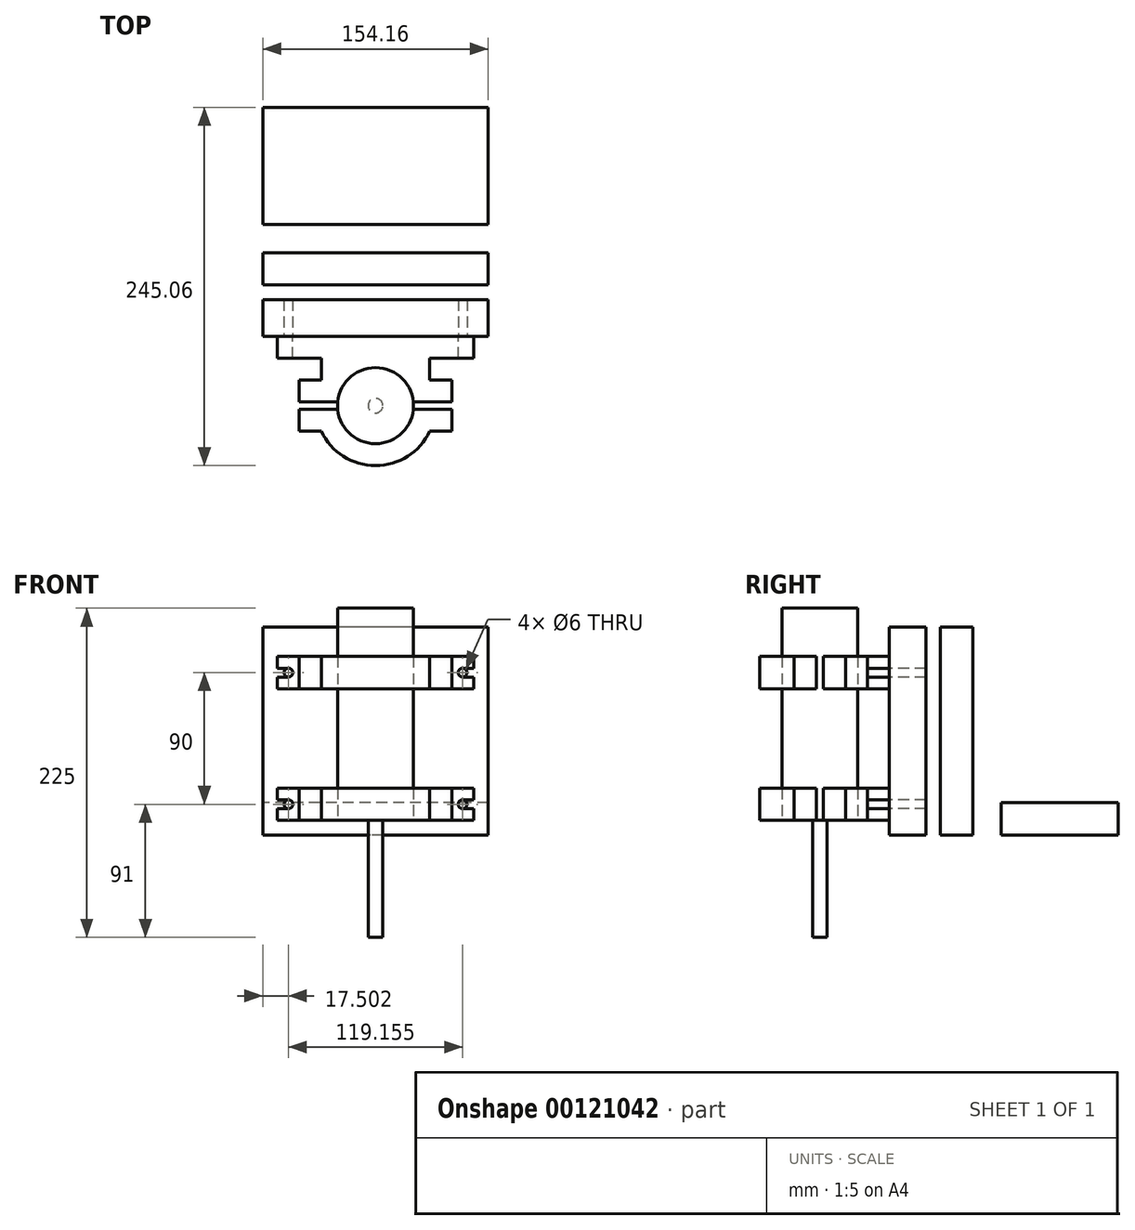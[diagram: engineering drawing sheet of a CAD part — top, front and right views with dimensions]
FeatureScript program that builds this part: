
annotation { "Feature Type Name" : "Feature", "Feature Type Description" : "" }
export const myFeature = defineFeature(function(context is Context, id is Id, definition is map)
    precondition{}
    {
        {
            var Q0;
            Q0=qCreatedBy(makeId("Top.planeOp"),FACE);
            var sketch = newSketch(context, id + "F0", { "sketchPlane" : qUnion([Q0])});
            skCircle(sketch, "E0", {"center": v(0, 0) * mm, "radius": 5 * mm});
            skCircle(sketch, "E1", {"center": v(0, 0) * mm, "radius": 26 * mm});
            skSolve(sketch);
        }
        {
            var Q0;
            Q0=makeQuery(id+"F0.imprint","IMPRINT",FACE,{"disambiguationData":[TD([[makeQuery(id+"F0.imprint","IMPRINT",EDGE,{"derivedFrom":sQuery(id+"F0.wireOp",EDGE,"E0")}),-1.0]])]});
            var Q1;
            Q1=makeQuery(id+"F0.imprint","IMPRINT",FACE,{"disambiguationData":[TD([[makeQuery(id+"F0.imprint","IMPRINT",EDGE,{"derivedFrom":sQuery(id+"F0.wireOp",EDGE,"E0")}),1.0]])]});
            extrude(context, id + "F1", {"entities" : qUnion([Q0, Q1]), "depth" : 145 * mm});
        }
        {
            var Q0;
            Q0=makeQuery(id+"F0.imprint","IMPRINT",FACE,{"disambiguationData":[TD([[makeQuery(id+"F0.imprint","IMPRINT",EDGE,{"derivedFrom":sQuery(id+"F0.wireOp",EDGE,"E0")}),1.0]])]});
            extrude(context, id + "F2", {"entities" : qUnion([Q0]), "operationType" : NewBodyOperationType.ADD, "oppositeDirection" : true, "depth" : 80 * mm});
        }
        {
            var Q0;
            Q0=qCreatedBy(makeId("Top.planeOp"),FACE);
            var sketch = newSketch(context, id + "F3", { "sketchPlane" : qUnion([Q0])});
            skArc(sketch, "E2.0", {"start": v(-25.88, -2.5) * mm, "mid": v(0, -26) * mm, "end": v(25.88, -2.5) * mm});
            skLineSegment(sketch, "E3", {"start": v(-25.88, -2.5) * mm, "end": v(-52.08, -2.5) * mm});
            skLineSegment(sketch, "E4", {"start": v(-52.08, -2.5) * mm, "end": v(-52.08, -17.5) * mm});
            skLineSegment(sketch, "E5", {"start": v(-52.08, -17.5) * mm, "end": v(-37.08, -17.5) * mm});
            skArc(sketch, "E6", {"start": v(-37.08, -17.5) * mm, "mid": v(-21.95, -34.63) * mm, "end": v(0, -41) * mm});
            skLineSegment(sketch, "E7", {"start": v(-25.88, 2.5) * mm, "end": v(-52.08, 2.5) * mm});
            skLineSegment(sketch, "E8", {"start": v(-52.08, 2.5) * mm, "end": v(-52.08, 17.5) * mm});
            skLineSegment(sketch, "E9", {"start": v(-52.08, 17.5) * mm, "end": v(-37.08, 17.5) * mm});
            skLineSegment(sketch, "E10", {"start": v(-37.08, 17.5) * mm, "end": v(-37.08, 32.5) * mm});
            skLineSegment(sketch, "E11", {"start": v(-37.08, 32.5) * mm, "end": v(-67.08, 32.5) * mm});
            skLineSegment(sketch, "E12", {"start": v(-67.08, 32.5) * mm, "end": v(-67.08, 47.5) * mm});
            skLineSegment(sketch, "E13", {"start": v(-67.08, 47.5) * mm, "end": v(0, 47.5) * mm});
            skLineSegment(sketch, "E14.MirrorCS", {"start": v(52.08, 17.5) * mm, "end": v(37.08, 17.5) * mm});
            skLineSegment(sketch, "E15.MirrorCS", {"start": v(37.08, 17.5) * mm, "end": v(37.08, 32.5) * mm});
            skLineSegment(sketch, "E16.MirrorCS", {"start": v(52.08, 2.5) * mm, "end": v(52.08, 17.5) * mm});
            skLineSegment(sketch, "E17.MirrorCS", {"start": v(37.08, 32.5) * mm, "end": v(67.08, 32.5) * mm});
            skLineSegment(sketch, "E18.MirrorCS", {"start": v(25.88, 2.5) * mm, "end": v(52.08, 2.5) * mm});
            skLineSegment(sketch, "E19.MirrorCS", {"start": v(67.08, 32.5) * mm, "end": v(67.08, 47.5) * mm});
            skLineSegment(sketch, "E20.MirrorCS", {"start": v(52.08, -17.5) * mm, "end": v(37.08, -17.5) * mm});
            skLineSegment(sketch, "E21.MirrorCS", {"start": v(52.08, -2.5) * mm, "end": v(52.08, -17.5) * mm});
            skLineSegment(sketch, "E22.MirrorCS", {"start": v(25.88, -2.5) * mm, "end": v(52.08, -2.5) * mm});
            skLineSegment(sketch, "E23.MirrorCS", {"start": v(67.08, 47.5) * mm, "end": v(0, 47.5) * mm});
            skArc(sketch, "E24.MirrorCS", {"start": v(37.08, -17.5) * mm, "mid": v(21.95, -34.63) * mm, "end": v(0, -41) * mm});
            skArc(sketch, "E25.trimOffspring", {"start": v(25.88, 2.5) * mm, "mid": v(0, 26) * mm, "end": v(-25.88, 2.5) * mm});
            skSolve(sketch);
        }
        {
            var Q0;
            Q0 = qSketchRegion(id + "F3", true);
            extrude(context, id + "F4", {"entities" : qUnion([Q0]), "depth" : 22 * mm});
        }
        {
            var Q0;
            Q0=makeQuery(id+"F4.opExtrude","SWEPT_FACE",FACE,{"disambiguationData":[OSD([sQuery(id+"F3.wireOp",EDGE,"E13"),sQuery(id+"F3.wireOp",EDGE,"E23.MirrorCS")])]});
            var sketch = newSketch(context, id + "F5", { "sketchPlane" : qUnion([Q0])});
            skLineSegment(sketch, "E26.0", {"start": v(-52.08, 22) * mm, "end": v(-52.08, 0) * mm, "construction": true});
            skLineSegment(sketch, "E27.0.0", {"start": v(-67.08, 0) * mm, "end": v(-62.58, 0) * mm, "construction": true});
            skLineSegment(sketch, "E27.0.1", {"start": v(67.08, 0) * mm, "end": v(67.08, 22) * mm, "construction": true});
            skLineSegment(sketch, "E27.0.2", {"start": v(67.08, 22) * mm, "end": v(-67.08, 22) * mm, "construction": true});
            skLineSegment(sketch, "E27.0.3", {"start": v(-67.08, 22) * mm, "end": v(-67.08, 0) * mm, "construction": true});
            skLineSegment(sketch, "E28", {"start": v(-67.08, 11) * mm, "end": v(-52.08, 11) * mm, "construction": true});
            skArc(sketch, "E29", {"start": v(-56.58, 11) * mm, "mid": v(-59.58, 14) * mm, "end": v(-62.58, 11) * mm});
            skLineSegment(sketch, "E30", {"start": v(-56.58, 0) * mm, "end": v(-62.58, 0) * mm});
            skArc(sketch, "E31.MirrorCS", {"start": v(56.58, 11) * mm, "mid": v(59.58, 14) * mm, "end": v(62.58, 11) * mm});
            skCircle(sketch, "E32", {"center": v(-59.58, 11) * mm, "radius": 3 * mm});
            skLineSegment(sketch, "E33.trimOffspring", {"start": v(-56.58, 0) * mm, "end": v(67.08, 0) * mm, "construction": true});
            skLineSegment(sketch, "E34", {"start": v(-59.58, 14) * mm, "end": v(-67.08, 14) * mm});
            skLineSegment(sketch, "E35", {"start": v(-59.58, 8) * mm, "end": v(-67.08, 8) * mm});
            skLineSegment(sketch, "E36", {"start": v(-67.08, 8) * mm, "end": v(-67.08, 14) * mm});
            skLineSegment(sketch, "E37.MirrorCS", {"start": v(67.08, 8) * mm, "end": v(67.08, 14) * mm});
            skLineSegment(sketch, "E38.MirrorCS", {"start": v(59.58, 8) * mm, "end": v(67.08, 8) * mm});
            skLineSegment(sketch, "E39.MirrorCS", {"start": v(67.08, 22) * mm, "end": v(67.08, 0) * mm, "construction": true});
            skLineSegment(sketch, "E40.MirrorCS", {"start": v(59.58, 14) * mm, "end": v(67.08, 14) * mm});
            skCircle(sketch, "E41.MirrorC", {"center": v(59.58, 11) * mm, "radius": 3 * mm});
            skLineSegment(sketch, "E42.MirrorCS", {"start": v(67.08, 11) * mm, "end": v(52.08, 11) * mm, "construction": true});
            skSolve(sketch);
        }
        {
            var Q0;
            Q0 = qSketchRegion(id + "F5", true);
            extrude(context, id + "F6", {"entities" : qUnion([Q0]), "operationType" : NewBodyOperationType.REMOVE, "endBound" : BoundingType.THROUGH_ALL, "oppositeDirection" : true, "depth" : 25 * mm});
        }
        {
            var Q0;
            Q0=makeQuery(id+"F4.opExtrude","SWEPT_BODY",BODY,{"disambiguationData":[OSD([sQuery(id+"F3.wireOp",EDGE,"E2.0"),sQuery(id+"F3.wireOp",EDGE,"E3"),sQuery(id+"F3.wireOp",EDGE,"E4"),sQuery(id+"F3.wireOp",EDGE,"E5"),sQuery(id+"F3.wireOp",EDGE,"E6"),sQuery(id+"F3.wireOp",EDGE,"E20.MirrorCS"),sQuery(id+"F3.wireOp",EDGE,"E21.MirrorCS"),sQuery(id+"F3.wireOp",EDGE,"E22.MirrorCS"),sQuery(id+"F3.wireOp",EDGE,"E24.MirrorCS")])]});
            transform(context, id + "F7", {"entities" : qUnion([Q0]), "transformType" : TransformType.TRANSLATION_3D, "dx" : 0 * mm, "dy" : 0 * mm, "dz" : 90 * mm, "makeCopy" : true});
        }
        {
            var Q0;
            Q0=makeQuery(id+"F4.opExtrude","SWEPT_BODY",BODY,{"disambiguationData":[OSD([sQuery(id+"F3.wireOp",EDGE,"E7"),sQuery(id+"F3.wireOp",EDGE,"E8"),sQuery(id+"F3.wireOp",EDGE,"E9"),sQuery(id+"F3.wireOp",EDGE,"E10"),sQuery(id+"F3.wireOp",EDGE,"E11"),sQuery(id+"F3.wireOp",EDGE,"E12"),sQuery(id+"F3.wireOp",EDGE,"E13"),sQuery(id+"F3.wireOp",EDGE,"E14.MirrorCS"),sQuery(id+"F3.wireOp",EDGE,"E15.MirrorCS"),sQuery(id+"F3.wireOp",EDGE,"E16.MirrorCS"),sQuery(id+"F3.wireOp",EDGE,"E17.MirrorCS"),sQuery(id+"F3.wireOp",EDGE,"E18.MirrorCS"),sQuery(id+"F3.wireOp",EDGE,"E19.MirrorCS"),sQuery(id+"F3.wireOp",EDGE,"E23.MirrorCS"),sQuery(id+"F3.wireOp",EDGE,"E25.trimOffspring")])]});
            transform(context, id + "F8", {"entities" : qUnion([Q0]), "transformType" : TransformType.TRANSLATION_3D, "dx" : 0 * mm, "dy" : 0 * mm, "dz" : 90 * mm, "makeCopy" : true});
        }
        {
            var Q0;
            Q0=makeQuery(id+"F8.opPattern","COPY",FACE,{"derivedFrom":makeQuery(id+"F4.opExtrude","SWEPT_FACE",FACE,{"disambiguationData":[OSD([sQuery(id+"F3.wireOp",EDGE,"E13"),sQuery(id+"F3.wireOp",EDGE,"E23.MirrorCS")])]}),"instanceName":"1"});
            var sketch = newSketch(context, id + "F9", { "sketchPlane" : qUnion([Q0])});
            skLineSegment(sketch, "E43", {"start": v(0, 132) * mm, "end": v(-77.08, 132) * mm});
            skLineSegment(sketch, "E44", {"start": v(-77.08, 132) * mm, "end": v(-77.08, -10) * mm});
            skLineSegment(sketch, "E45", {"start": v(-77.08, -10) * mm, "end": v(0, -10) * mm});
            skLineSegment(sketch, "E46.MirrorCS", {"start": v(77.08, -10) * mm, "end": v(0, -10) * mm});
            skLineSegment(sketch, "E47.MirrorCS", {"start": v(77.08, 132) * mm, "end": v(77.08, -10) * mm});
            skLineSegment(sketch, "E48.MirrorCS", {"start": v(0, 132) * mm, "end": v(77.08, 132) * mm});
            skLineSegment(sketch, "E49.0.0", {"start": v(-67.08, 90) * mm, "end": v(67.08, 90) * mm, "construction": true});
            skLineSegment(sketch, "E49.0.1", {"start": v(67.08, 90) * mm, "end": v(67.08, 98) * mm, "construction": true});
            skLineSegment(sketch, "E49.0.2", {"start": v(67.08, 112) * mm, "end": v(-67.08, 112) * mm, "construction": true});
            skLineSegment(sketch, "E49.0.3", {"start": v(-67.08, 112) * mm, "end": v(-67.08, 90) * mm, "construction": true});
            skLineSegment(sketch, "E50.0.0", {"start": v(-67.08, 0) * mm, "end": v(67.08, 0) * mm, "construction": true});
            skLineSegment(sketch, "E50.0.1", {"start": v(67.08, 8) * mm, "end": v(67.08, 14) * mm, "construction": true});
            skLineSegment(sketch, "E50.0.2", {"start": v(67.08, 22) * mm, "end": v(-67.08, 22) * mm, "construction": true});
            skLineSegment(sketch, "E50.0.3", {"start": v(-67.08, 22) * mm, "end": v(-67.08, 0) * mm, "construction": true});
            skLineSegment(sketch, "E51", {"start": v(-67.08, 101) * mm, "end": v(67.08, 101) * mm, "construction": true});
            skLineSegment(sketch, "E52", {"start": v(-67.08, 11) * mm, "end": v(67.08, 11) * mm, "construction": true});
            skCircle(sketch, "E53", {"center": v(-59.58, 101) * mm, "radius": 3 * mm});
            skCircle(sketch, "E54", {"center": v(-59.58, 11) * mm, "radius": 3 * mm});
            skLineSegment(sketch, "E55.0", {"start": v(-52.08, 112) * mm, "end": v(-52.08, 90) * mm, "construction": true});
            skLineSegment(sketch, "E56", {"start": v(-67.08, 101) * mm, "end": v(-52.08, 101) * mm, "construction": true});
            skCircle(sketch, "E57.MirrorC", {"center": v(59.58, 101) * mm, "radius": 3 * mm});
            skCircle(sketch, "E58.MirrorC", {"center": v(59.58, 11) * mm, "radius": 3 * mm});
            skSolve(sketch);
        }
        {
            var Q0;
            Q0 = qSketchRegion(id + "F9", true);
            extrude(context, id + "F10", {"entities" : qUnion([Q0]), "depth" : 25 * mm});
        }
        {
            var Q0;
            Q0=makeQuery(id+"F10.opExtrude","CAP_FACE",FACE,{"disambiguationData":[OSD([sQuery(id+"F9.wireOp",EDGE,"E43"),sQuery(id+"F9.wireOp",EDGE,"E44"),sQuery(id+"F9.wireOp",EDGE,"E45"),sQuery(id+"F9.wireOp",EDGE,"E46.MirrorCS"),sQuery(id+"F9.wireOp",EDGE,"E47.MirrorCS"),sQuery(id+"F9.wireOp",EDGE,"E48.MirrorCS"),sQuery(id+"F9.wireOp",EDGE,"E53"),sQuery(id+"F9.wireOp",EDGE,"E54"),sQuery(id+"F9.wireOp",EDGE,"E57.MirrorC"),sQuery(id+"F9.wireOp",EDGE,"E58.MirrorC")])],"isStart":false});
            cPlane(context, id + "F11", {"entities" : qUnion([Q0]), "cplaneType" : CPlaneType.OFFSET, "offset" : 10 * mm, "width" : 150 * mm, "height" : 150 * mm});
        }
        {
            var Q0;
            Q0=qCreatedBy(id+"F11.planeOp",FACE);
            var sketch = newSketch(context, id + "F12", { "sketchPlane" : qUnion([Q0])});
            skLineSegment(sketch, "E59.0", {"start": v(-77.08, 132) * mm, "end": v(77.08, 132) * mm});
            skLineSegment(sketch, "E60.0", {"start": v(77.08, 132) * mm, "end": v(77.08, -10) * mm});
            skLineSegment(sketch, "E61.0", {"start": v(-77.08, -10) * mm, "end": v(77.08, -10) * mm});
            skLineSegment(sketch, "E62.0", {"start": v(-77.08, 132) * mm, "end": v(-77.08, -10) * mm});
            skSolve(sketch);
        }
        {
            var Q0;
            Q0 = qSketchRegion(id + "F12", true);
            extrude(context, id + "F13", {"entities" : qUnion([Q0]), "depth" : 22 * mm});
        }
        {
            var Q0;
            Q0=makeQuery(id+"F13.opExtrude","SWEPT_FACE",FACE,{"disambiguationData":[OSD([sQuery(id+"F12.wireOp",EDGE,"E61.0")])]});
            var sketch = newSketch(context, id + "F14", { "sketchPlane" : qUnion([Q0])});
            skLineSegment(sketch, "E63.bottom", {"start": v(77.08, -124.06) * mm, "end": v(-77.08, -124.06) * mm});
            skLineSegment(sketch, "E63.top", {"start": v(77.08, -204.06) * mm, "end": v(-77.08, -204.06) * mm});
            skLineSegment(sketch, "E63.left", {"start": v(77.08, -124.06) * mm, "end": v(77.08, -204.06) * mm});
            skLineSegment(sketch, "E63.right", {"start": v(-77.08, -124.06) * mm, "end": v(-77.08, -204.06) * mm});
            skSolve(sketch);
        }
        {
            var Q0;
            Q0 = qSketchRegion(id + "F14", true);
            extrude(context, id + "F15", {"entities" : qUnion([Q0]), "oppositeDirection" : true, "depth" : 22 * mm});
        }
    });
